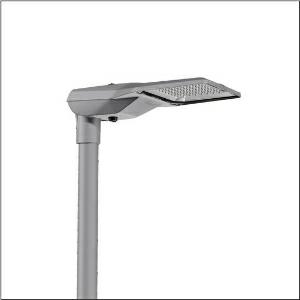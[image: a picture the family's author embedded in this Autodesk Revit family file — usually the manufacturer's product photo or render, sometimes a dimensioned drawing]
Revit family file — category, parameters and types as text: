
# Revit family: streetlight_sl_21_midi___st0_8a_5xe3c43t08lb_a4d4
name_source: partatom
category: Lighting Fixtures
units: mm (PartAtom-declared; Revit-internal decimal feet)

## family parameters
Cut with Voids When Loaded = No
Host = Face
Light Source = No
Part Type = Normal
Room Calculation Point = No
Round Connector Dimension = Use Diameter
Shared = No

## types (1)
- --- (1 x LED, 14950 lm, 99.6 W, 4000K)
    Apparent Load = 100 VA
    CIE Flux Codes = 38 75 97 100 100
    Color Rendering = 70
    Color Temperature = 4000K
    Default Elevation = 1800 mm
    Description = Streetlight SL 21 midi, mast luminaire, primary light control with lens, of PMMA, primary optical cover: cover, of toughened safety glass, transparent, light distribution: ST0.8a, light emission: direct distribution, primary light characteristic: asymmetric, installation type: side-entry, post-top, LED, High Power LED, rated luminous flux: 14.950lm, luminous efficacy: 150lm/W, light colour: 740, colour temperature: 4000K, control gear: D4i, control: overheat protection, constant luminous flux control, time-dependent luminous flux control, flexible luminous flux parameterisation, pre-setting: logarithmic dimming characteristic, mains connection: 230..240V, AC, 50/60Hz, start of lifetime: 100W, end of service life: 102W, reduction: 46W, luminaire housing, of diecast aluminium, powder-coated, SITECO metallic grey (DB 702S), corrosivity category C5 high according to DIN EN ISO 12944, please order mast flange separately, inclination adjustable: 0°, 5°, 10°, 15°, sealing non-destructively replaceable, multi-level sealing system, length: 644mm, width: 335mm, height: 110mm, mast flange for spigot size: 42mm (side-entry): 5XC10008XM4, 60/48mm (side-entry/post-top): 5XC10108XM2, 76/60mm (side-entry/post-top): 5XC10108XM1, mounting height: 4..8m, Smart Interface below and above, protection rating (complete): IP66, insulation class (complete): insulation class II (safety insulation), certification: CE, ENEC, ENEC+, VDE, impact resistance: IK10, permissible operating ambient temperature for outdoor applications: -40..+50°C, standard-compliant lighting for roads and squares, packaging unit: 1 piece

Light Distribution: ST0.8a
    Height = 111 mm
    Lamp = 1 x LED
    Lamp Light Flux = 14950 lm
    Lamp Power = 99.6 W
    Lamp count = 1
    Length = 644 mm
    Luminous efficacy = 150 lm/W
    Manufacturer = Siteco
    ModVariant = No
    Model = 5XE3C43T08LB
    Number of Poles = 1
    OnlyDefault = Yes
    Power Factor = 1
    Product Name = Streetlight SL 21 midi | ST0.8a
    Product group = mast luminaire | pylon top
    ProductGroupID = 6100
    Protection Class = Protection class II
    Protection Degree = IP 66
    RLX_Detail_Level = 1
    RLX_Emergency_Light_Flux = 0 lm
    RLX_Emergency_Type = 0
    RLX_Emergency_Type_DB = No
    RlxData = <blob elided: 26921 chars, md5=5ff6bc57>
    Socket = socket
    Standby Power = 0 W
    System Light Flux = 14950 lm
    System Power = 100 W
    Type Comments = factory setting: luminous flux: 100 % | dim-lin: 254 | 1020 mA
    Type Image = l_1004304.jpg
    URL = http://relux.com
    VarID = @adj_030969
    Voltage = 0 V
    Weight = 0.00 kg
    Width = 336 mm

## geometry (parser evidence)
native form markers: Blend x4, Sweep x11
no freeform markers — native parametric forms only
